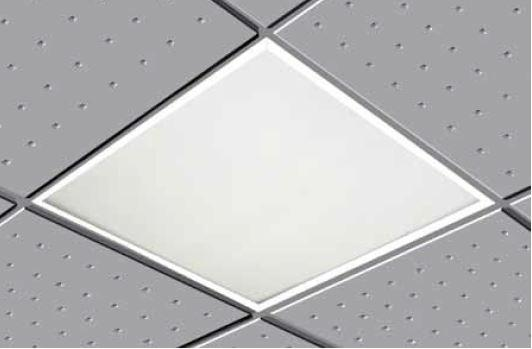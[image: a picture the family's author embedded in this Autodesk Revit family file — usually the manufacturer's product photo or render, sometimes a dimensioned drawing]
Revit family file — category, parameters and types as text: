
# Revit family: G 6060 OPL
name_source: partatom
category: Lighting Fixtures
revit_build: Autodesk Revit 2017 (Build: 20160225_1515(x64)
units: mm (PartAtom-declared; Revit-internal decimal feet)

## family parameters
Always vertical = Yes
Cut with Voids When Loaded = No
Host = Ceiling
Light Source = Yes
OmniClass Number = 23.80.70.11
OmniClass Title = Luminaries for Internal Lighting
Part Type = Normal
Room Calculation Point = No
Round Connector Dimension = Use Diameter
Shared = No

## types (4) — shared parameters
Color Filter = 16777215
Dimming Lamp Color Temperature Shift = <None>
Emit Shape Visible in Rendering = Yes
Emit from Rectangle Length = 570 mm  [stored 1.87008 ft]
Emit from Rectangle Width = 570 mm  [stored 1.87008 ft]
Light Source Symbol Size = 610 mm
Manufacturer = ARLIGHT
Type Image = G 6060 OPL.JPG

## per-type parameters (varying)
| type | Apparent Load | Wattage Comments |
| GOPL.6060.36.30 | 36 VA | 36 |
| GOPL.6060.36.40 | 36 VA | 36 |
| GOPL.6060.28.30 | 28 VA | 28 |
| GOPL.6060.28.40 | 28 VA | 28 |

note: [stored X ft] marks values corroborated as IEEE doubles in the binary element streams (Revit-internal decimal feet)

## geometry (parser evidence)
native form markers: Sweep x2
no freeform markers — native parametric forms only
